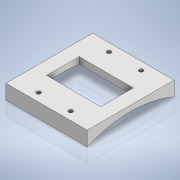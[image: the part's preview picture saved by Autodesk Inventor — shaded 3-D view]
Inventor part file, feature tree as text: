
AUTODESK INVENTOR PART (.ipt)
format: ipt  version: 2022 (Build 260153000, 153)  size: 158,720 bytes
history: native  units: mm
features: extrude x3, sketch x3, other x3, reference x1
ambient origin geometry x8: Origin, YZ Plane, XZ Plane, XY Plane, X Axis, Y Axis, Z Axis, Center Point
bodies: Solid1 (feature_tree)
feature tree (10):
  extrude  "Extrusion1"  Depth=16.0mm
  extrude  "Extrusion2"  Depth=6.0mm
  extrude  "Extrusion3"  Depth=10.0mm
  sketch  "Sketch1"  dims[d0=15.0mm d1=16.0mm]
  sketch  "Sketch2"  dims[d2=10.0mm d3=6.0mm]
  reference  "Reference1"
  sketch  "Sketch3"  dims[d4=2.5mm d5=5.0mm d6=0.75mm d7=4.5125mm d8=1.5mm d9=20.0mm d11=5.925mm d12=20.0mm d14=12.985mm d17=1.0mm d18=0.0mm d19=10.0mm d20=0.0mm d21=0.0mm d22=0.0mm]
  other  "<userpath>\Documents\Telescope\Telescope.iam"
  other  "Telescope.iam"
  other  "Aperture:1"
